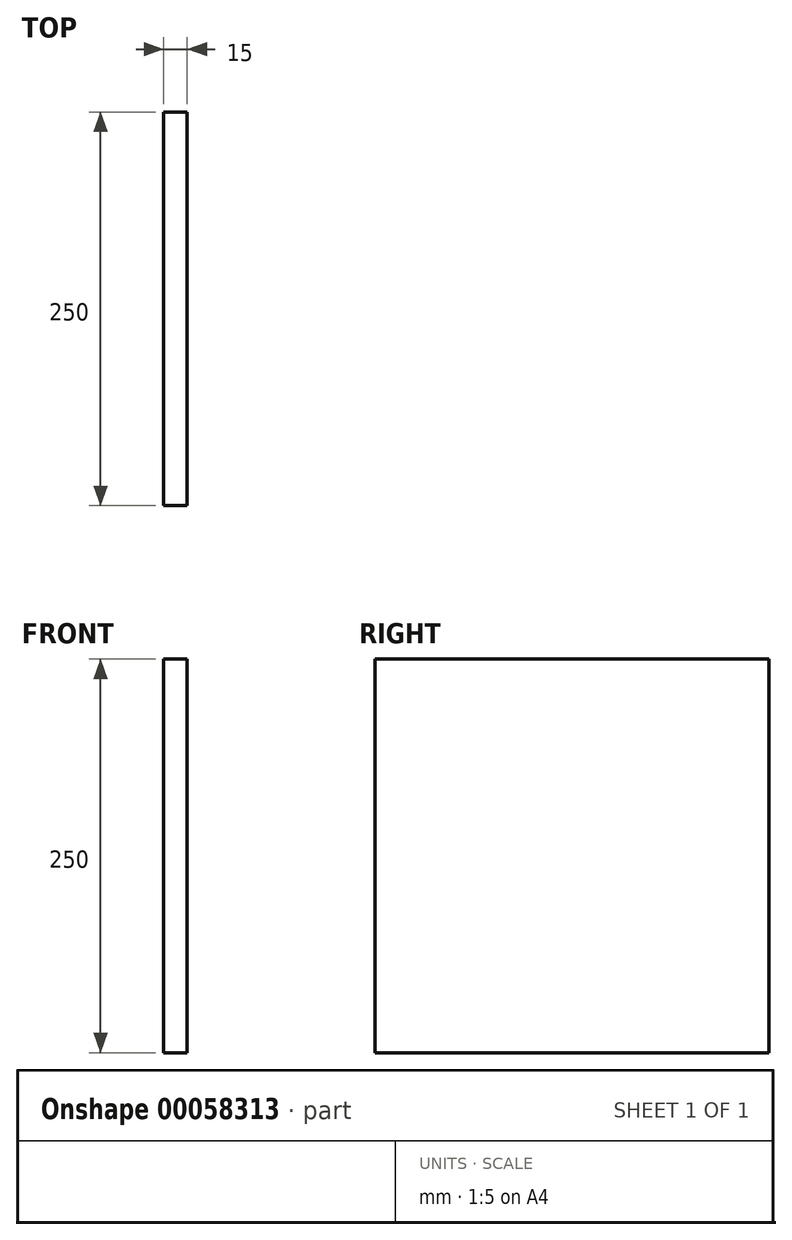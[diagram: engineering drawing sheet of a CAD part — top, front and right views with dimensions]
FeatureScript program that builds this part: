
annotation { "Feature Type Name" : "Feature", "Feature Type Description" : "" }
export const myFeature = defineFeature(function(context is Context, id is Id, definition is map)
    precondition{}
    {
        {
            var Q0;
            Q0=qCreatedBy(makeId("Right.planeOp"),FACE);
            var sketch = newSketch(context, id + "F0", { "sketchPlane" : qUnion([Q0])});
            skLineSegment(sketch, "E0.rect.bottom", {"start": v(125, -125) * mm, "end": v(-125, -125) * mm});
            skLineSegment(sketch, "E0.rect.top", {"start": v(125, 125) * mm, "end": v(-125, 125) * mm});
            skLineSegment(sketch, "E0.rect.left", {"start": v(125, -125) * mm, "end": v(125, 125) * mm});
            skLineSegment(sketch, "E0.rect.right", {"start": v(-125, -125) * mm, "end": v(-125, 125) * mm});
            skPoint(sketch, "E0.rect.middle", {"position": v(0, 0) * mm});
            skSolve(sketch);
        }
        {
            var Q0;
            Q0 = qSketchRegion(id + "F0", true);
            extrude(context, id + "F1", {"entities" : qUnion([Q0]), "depth" : 15 * mm});
        }
    });
